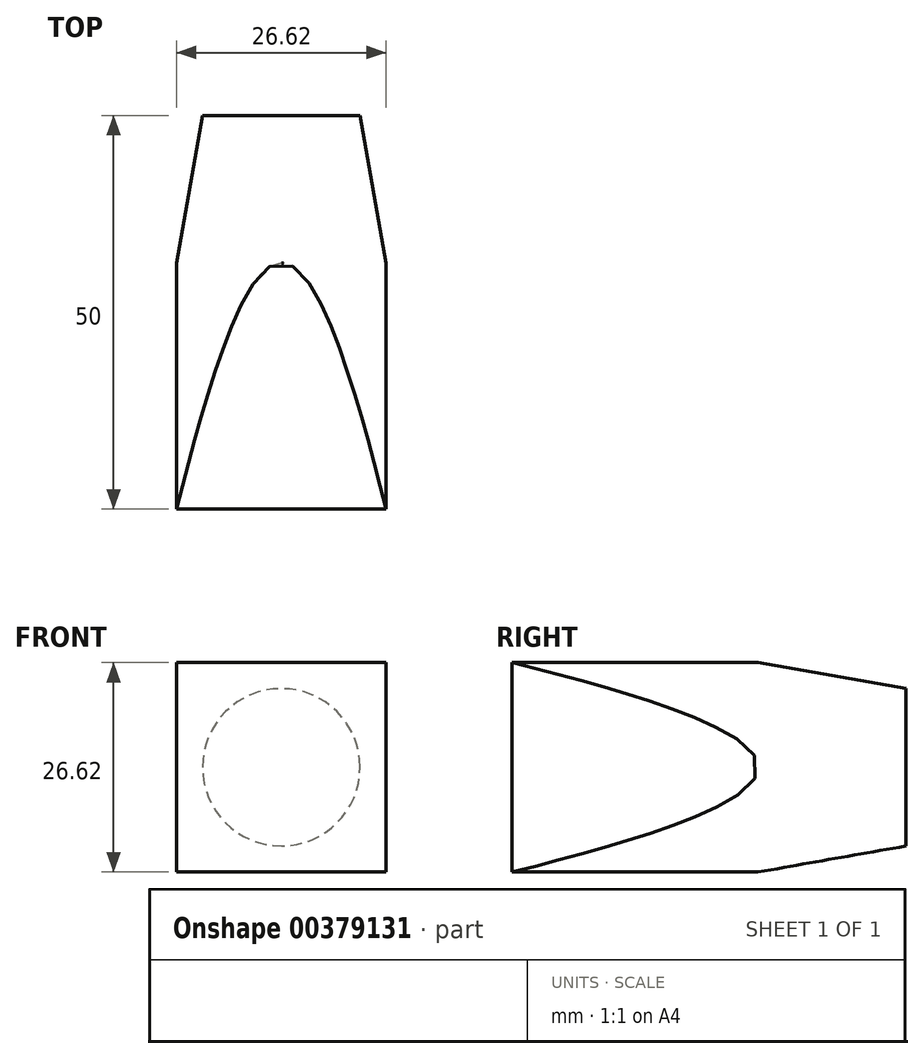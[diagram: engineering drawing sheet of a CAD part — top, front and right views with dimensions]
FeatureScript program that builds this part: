
annotation { "Feature Type Name" : "Feature", "Feature Type Description" : "" }
export const myFeature = defineFeature(function(context is Context, id is Id, definition is map)
    precondition{}
    {
        {
            var Q0;
            Q0=qCreatedBy(makeId("Front.planeOp"),FACE);
            var sketch = newSketch(context, id + "F0", { "sketchPlane" : qUnion([Q0])});
            skCircle(sketch, "E0", {"center": v(0, 0) * mm, "radius": 10 * mm});
            skSolve(sketch);
        }
        {
            var Q0;
            Q0=makeQuery(id+"F0.imprint","IMPRINT",FACE,{"disambiguationData":[TD([[makeQuery(id+"F0.imprint","IMPRINT",EDGE,{"derivedFrom":sQuery(id+"F0.wireOp",EDGE,"E0")}),1.0]])]});
            extrude(context, id + "F1", {"entities" : qUnion([Q0]), "depth" : 50 * mm, "hasDraft" : true, "draftAngle" : 10 * degree});
        }
        {
            var Q0;
            Q0=makeQuery(id+"F1.opExtrude","CAP_FACE",FACE,{"disambiguationData":[OSD([sQuery(id+"F0.wireOp",EDGE,"E0")])],"isStart":false});
            var sketch = newSketch(context, id + "F2", { "sketchPlane" : qUnion([Q0])});
            skLineSegment(sketch, "E1.bottom", {"start": v(13.3, -13.3) * mm, "end": v(-13.3, -13.3) * mm});
            skLineSegment(sketch, "E1.top", {"start": v(13.3, 13.3) * mm, "end": v(-13.3, 13.3) * mm});
            skLineSegment(sketch, "E1.left", {"start": v(13.3, -13.3) * mm, "end": v(13.3, 13.3) * mm});
            skLineSegment(sketch, "E1.right", {"start": v(-13.3, -13.3) * mm, "end": v(-13.3, 13.3) * mm});
            skPoint(sketch, "E1.middle", {"position": v(0, 0) * mm});
            skSolve(sketch);
        }
        {
            var Q0;
            Q0 = qSketchRegion(id + "F2", true);
            extrude(context, id + "F3", {"entities" : qUnion([Q0]), "operationType" : NewBodyOperationType.INTERSECT, "oppositeDirection" : true, "depth" : 50 * mm});
        }
    });
